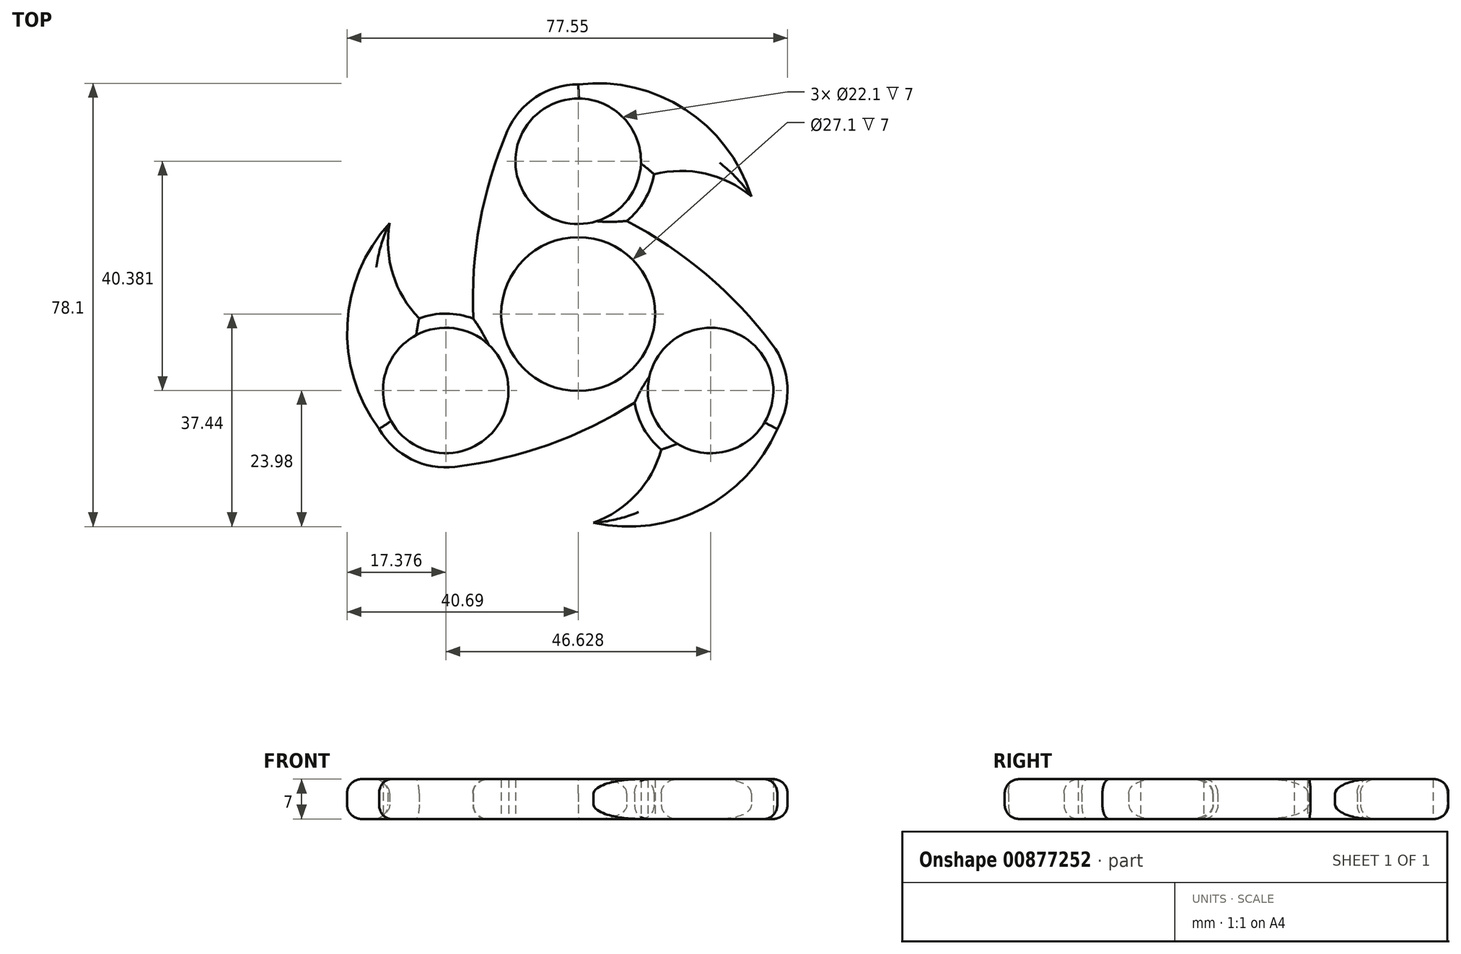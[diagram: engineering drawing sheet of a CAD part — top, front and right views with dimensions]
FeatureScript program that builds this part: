
annotation { "Feature Type Name" : "Feature", "Feature Type Description" : "" }
export const myFeature = defineFeature(function(context is Context, id is Id, definition is map)
    precondition{}
    {
        {
            var Q0;
            Q0=qCreatedBy(makeId("Top.planeOp"),FACE);
            var sketch = newSketch(context, id + "F0", { "sketchPlane" : qUnion([Q0])});
            skCircle(sketch, "E0", {"center": v(0, 0) * mm, "radius": 11.05 * mm});
            skCircle(sketch, "E1", {"center": v(0, 0) * mm, "radius": 13.55 * mm});
            skCircle(sketch, "E2", {"center": v(0, 26.92) * mm, "radius": 11.05 * mm});
            skArc(sketch, "E3", {"start": v(8.55, 16.4) * mm, "mid": v(11.7, 20.08) * mm, "end": v(13.35, 24.62) * mm});
            skCircle(sketch, "E4.1.0", {"center": v(-23.31, -13.46) * mm, "radius": 11.05 * mm});
            skArc(sketch, "E4.1.1", {"start": v(-18.48, -0.8) * mm, "mid": v(-23.23, 0.09) * mm, "end": v(-28, -0.74) * mm});
            skCircle(sketch, "E4.2.0", {"center": v(23.31, -13.46) * mm, "radius": 11.05 * mm});
            skArc(sketch, "E5", {"start": v(30.48, 20.73) * mm, "mid": v(18.8, 36.09) * mm, "end": v(0, 40.47) * mm});
            skArc(sketch, "E6", {"start": v(30.48, 20.73) * mm, "mid": v(22.39, 24.74) * mm, "end": v(13.35, 24.62) * mm});
            skArc(sketch, "E7.1.0", {"start": v(-33.2, 16.03) * mm, "mid": v(-32.62, 7.01) * mm, "end": v(-28, -0.74) * mm});
            skArc(sketch, "E7.1.1", {"start": v(-33.2, 16.03) * mm, "mid": v(-40.65, -1.77) * mm, "end": v(-35.05, -20.24) * mm});
            skArc(sketch, "E7.2.0", {"start": v(2.71, -36.76) * mm, "mid": v(10.24, -31.76) * mm, "end": v(14.64, -23.87) * mm});
            skArc(sketch, "E7.2.1", {"start": v(2.71, -36.76) * mm, "mid": v(21.86, -34.32) * mm, "end": v(35.05, -20.24) * mm});
            skPoint(sketch, "E8.orphan", {"position": v(10.56, 23.67) * mm});
            skPoint(sketch, "E9.orphan", {"position": v(15.22, -20.98) * mm});
            skPoint(sketch, "E10.orphan", {"position": v(-25.78, -2.69) * mm});
            skArc(sketch, "E11", {"start": v(-18.48, -0.79) * mm, "mid": v(-18.48, -0.8) * mm, "end": v(-18.48, -0.8) * mm});
            skArc(sketch, "E12.trimOffspring", {"start": v(8.56, 16.4) * mm, "mid": v(8.55, 16.4) * mm, "end": v(8.55, 16.4) * mm});
            skArc(sketch, "E13.trimOffspring", {"start": v(9.92, -15.61) * mm, "mid": v(9.93, -15.6) * mm, "end": v(9.93, -15.6) * mm});
            skArc(sketch, "E14.trimOffspring", {"start": v(9.93, -15.6) * mm, "mid": v(11.54, -20.17) * mm, "end": v(14.64, -23.87) * mm});
            skArc(sketch, "E15.trimOffspring", {"start": v(-35.05, -20.24) * mm, "mid": v(-29.37, -25.58) * mm, "end": v(-21.69, -26.91) * mm});
            skArc(sketch, "E16.trimOffspring", {"start": v(0, 40.47) * mm, "mid": v(-7.47, 38.23) * mm, "end": v(-12.46, 32.24) * mm});
            skArc(sketch, "E17", {"start": v(-12.46, 32.24) * mm, "mid": v(-17.32, 16.06) * mm, "end": v(-18.48, -0.79) * mm});
            skArc(sketch, "E18.1.0", {"start": v(-21.69, -26.91) * mm, "mid": v(-5.25, -23.03) * mm, "end": v(9.92, -15.61) * mm});
            skArc(sketch, "E18.2.0", {"start": v(34.15, -5.32) * mm, "mid": v(22.57, 6.97) * mm, "end": v(8.56, 16.4) * mm});
            skArc(sketch, "E19.trimOffspring", {"start": v(35.05, -20.24) * mm, "mid": v(36.84, -12.64) * mm, "end": v(34.15, -5.32) * mm});
            skSolve(sketch);
        }
        {
            var Q0;
            Q0=makeQuery(id+"F0.imprint","IMPRINT",FACE,{"disambiguationData":[TD([[makeQuery(id+"F0.imprint","IMPRINT",EDGE,{"derivedFrom":sQuery(id+"F0.wireOp",EDGE,"E1")}),-1.0]])]});
            extrude(context, id + "F1", {"entities" : qUnion([Q0]), "depth" : 7 * mm, "offsetDistance" : 25 * mm});
        }
        {
            var Q0;
            Q0=makeQuery(id+"F1.opExtrude","CAP_EDGE",EDGE,{"disambiguationData":[OSD([sQuery(id+"F0.wireOp",EDGE,"E5")])],"isStart":false});
            var Q1;
            Q1=makeQuery(id+"F1.opExtrude","CAP_EDGE",EDGE,{"disambiguationData":[OSD([sQuery(id+"F0.wireOp",EDGE,"E6")])],"isStart":false});
            var Q2;
            Q2=makeQuery(id+"F1.opExtrude","CAP_EDGE",EDGE,{"disambiguationData":[OSD([sQuery(id+"F0.wireOp",EDGE,"E3")])],"isStart":false});
            var Q3;
            Q3=makeQuery(id+"F1.opExtrude","CAP_EDGE",EDGE,{"disambiguationData":[OSD([sQuery(id+"F0.wireOp",EDGE,"E18.2.0")])],"isStart":false});
            var Q4;
            Q4=makeQuery(id+"F1.opExtrude","CAP_EDGE",EDGE,{"disambiguationData":[OSD([sQuery(id+"F0.wireOp",EDGE,"E19.trimOffspring")])],"isStart":false});
            var Q5;
            Q5=makeQuery(id+"F1.opExtrude","CAP_EDGE",EDGE,{"disambiguationData":[OSD([sQuery(id+"F0.wireOp",EDGE,"E7.2.1")])],"isStart":false});
            var Q6;
            Q6=makeQuery(id+"F1.opExtrude","CAP_EDGE",EDGE,{"disambiguationData":[OSD([sQuery(id+"F0.wireOp",EDGE,"E7.2.0")])],"isStart":false});
            var Q7;
            Q7=makeQuery(id+"F1.opExtrude","CAP_EDGE",EDGE,{"disambiguationData":[OSD([sQuery(id+"F0.wireOp",EDGE,"E14.trimOffspring")])],"isStart":false});
            var Q8;
            Q8=makeQuery(id+"F1.opExtrude","CAP_EDGE",EDGE,{"disambiguationData":[OSD([sQuery(id+"F0.wireOp",EDGE,"E18.1.0")])],"isStart":false});
            var Q9;
            Q9=makeQuery(id+"F1.opExtrude","CAP_EDGE",EDGE,{"disambiguationData":[OSD([sQuery(id+"F0.wireOp",EDGE,"E15.trimOffspring")])],"isStart":false});
            var Q10;
            Q10=makeQuery(id+"F1.opExtrude","CAP_EDGE",EDGE,{"disambiguationData":[OSD([sQuery(id+"F0.wireOp",EDGE,"E7.1.1")])],"isStart":false});
            var Q11;
            Q11=makeQuery(id+"F1.opExtrude","CAP_EDGE",EDGE,{"disambiguationData":[OSD([sQuery(id+"F0.wireOp",EDGE,"E7.1.0")])],"isStart":false});
            var Q12;
            Q12=makeQuery(id+"F1.opExtrude","CAP_EDGE",EDGE,{"disambiguationData":[OSD([sQuery(id+"F0.wireOp",EDGE,"E4.1.1")])],"isStart":false});
            var Q13;
            Q13=makeQuery(id+"F1.opExtrude","CAP_EDGE",EDGE,{"disambiguationData":[OSD([sQuery(id+"F0.wireOp",EDGE,"E17")])],"isStart":false});
            var Q14;
            Q14=makeQuery(id+"F1.opExtrude","CAP_EDGE",EDGE,{"disambiguationData":[OSD([sQuery(id+"F0.wireOp",EDGE,"E16.trimOffspring")])],"isStart":false});
            fillet(context, id + "F2", {"entities" : qUnion([Q0, Q1, Q2, Q3, Q4, Q5, Q6, Q7, Q8, Q9, Q10, Q11, Q12, Q13, Q14]), "radius" : 2.5 * mm, "tangentPropagation" : true, "allowEdgeOverflow" : false});
        }
        {
            var Q0;
            Q0=makeQuery(id+"F1.opExtrude","CAP_EDGE",EDGE,{"disambiguationData":[OSD([sQuery(id+"F0.wireOp",EDGE,"E18.1.0")])],"isStart":true});
            var Q1;
            Q1=makeQuery(id+"F1.opExtrude","CAP_EDGE",EDGE,{"disambiguationData":[OSD([sQuery(id+"F0.wireOp",EDGE,"E15.trimOffspring")])],"isStart":true});
            var Q2;
            Q2=makeQuery(id+"F1.opExtrude","CAP_EDGE",EDGE,{"disambiguationData":[OSD([sQuery(id+"F0.wireOp",EDGE,"E7.1.1")])],"isStart":true});
            var Q3;
            Q3=makeQuery(id+"F1.opExtrude","CAP_EDGE",EDGE,{"disambiguationData":[OSD([sQuery(id+"F0.wireOp",EDGE,"E7.2.1")])],"isStart":true});
            var Q4;
            Q4=makeQuery(id+"F1.opExtrude","CAP_EDGE",EDGE,{"disambiguationData":[OSD([sQuery(id+"F0.wireOp",EDGE,"E19.trimOffspring")])],"isStart":true});
            var Q5;
            Q5=makeQuery(id+"F1.opExtrude","CAP_EDGE",EDGE,{"disambiguationData":[OSD([sQuery(id+"F0.wireOp",EDGE,"E18.2.0")])],"isStart":true});
            var Q6;
            Q6=makeQuery(id+"F1.opExtrude","CAP_EDGE",EDGE,{"disambiguationData":[OSD([sQuery(id+"F0.wireOp",EDGE,"E3")])],"isStart":true});
            var Q7;
            Q7=makeQuery(id+"F1.opExtrude","CAP_EDGE",EDGE,{"disambiguationData":[OSD([sQuery(id+"F0.wireOp",EDGE,"E6")])],"isStart":true});
            var Q8;
            Q8=makeQuery(id+"F1.opExtrude","CAP_EDGE",EDGE,{"disambiguationData":[OSD([sQuery(id+"F0.wireOp",EDGE,"E5")])],"isStart":true});
            var Q9;
            Q9=makeQuery(id+"F1.opExtrude","CAP_EDGE",EDGE,{"disambiguationData":[OSD([sQuery(id+"F0.wireOp",EDGE,"E16.trimOffspring")])],"isStart":true});
            var Q10;
            Q10=makeQuery(id+"F1.opExtrude","CAP_EDGE",EDGE,{"disambiguationData":[OSD([sQuery(id+"F0.wireOp",EDGE,"E17")])],"isStart":true});
            var Q11;
            Q11=makeQuery(id+"F1.opExtrude","CAP_EDGE",EDGE,{"disambiguationData":[OSD([sQuery(id+"F0.wireOp",EDGE,"E7.1.0")])],"isStart":true});
            var Q12;
            Q12=makeQuery(id+"F1.opExtrude","CAP_EDGE",EDGE,{"disambiguationData":[OSD([sQuery(id+"F0.wireOp",EDGE,"E4.1.1")])],"isStart":true});
            var Q13;
            Q13=makeQuery(id+"F1.opExtrude","CAP_EDGE",EDGE,{"disambiguationData":[OSD([sQuery(id+"F0.wireOp",EDGE,"E14.trimOffspring")])],"isStart":true});
            var Q14;
            Q14=makeQuery(id+"F1.opExtrude","CAP_EDGE",EDGE,{"disambiguationData":[OSD([sQuery(id+"F0.wireOp",EDGE,"E7.2.0")])],"isStart":true});
            fillet(context, id + "F3", {"entities" : qUnion([Q0, Q1, Q2, Q3, Q4, Q5, Q6, Q7, Q8, Q9, Q10, Q11, Q12, Q13, Q14]), "radius" : 2.5 * mm, "tangentPropagation" : true, "allowEdgeOverflow" : false});
        }
    });
